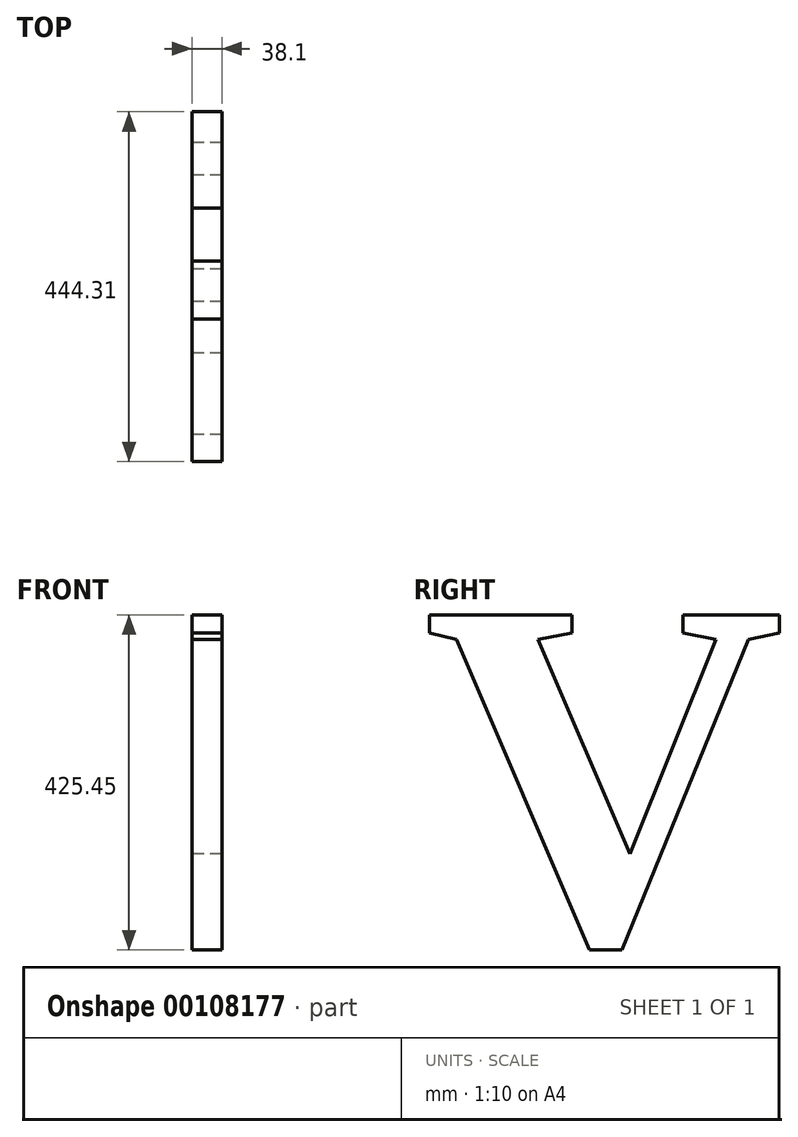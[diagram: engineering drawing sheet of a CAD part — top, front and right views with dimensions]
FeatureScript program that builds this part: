
annotation { "Feature Type Name" : "Feature", "Feature Type Description" : "" }
export const myFeature = defineFeature(function(context is Context, id is Id, definition is map)
    precondition{}
    {
        {
            var Q0;
            Q0=qCreatedBy(makeId("Right.planeOp"),FACE);
            var sketch = newSketch(context, id + "F0", { "sketchPlane" : qUnion([Q0])});
            skText(sketch, "E0", { "text": "V", "fontName": "Tinos-Bold.ttf"});
            const initialGuessF0  = {"E0": [-0.49113, 0, 1, 0, 0.4572]};
            skSetInitialGuess(sketch, initialGuessF0);
            skSolve(sketch);
        }
        {
            var Q0;
            Q0 = qSketchRegion(id + "F0", true);
            extrude(context, id + "F1", {"entities" : qUnion([Q0]), "depth" : 38.1 * mm});
        }
    });
